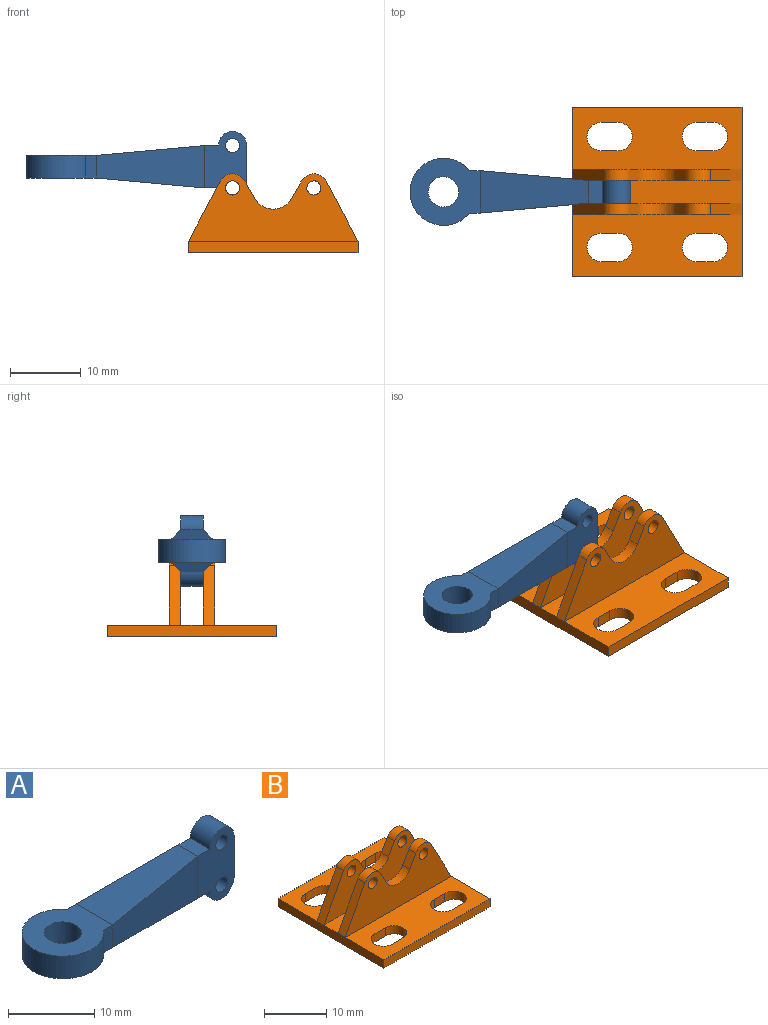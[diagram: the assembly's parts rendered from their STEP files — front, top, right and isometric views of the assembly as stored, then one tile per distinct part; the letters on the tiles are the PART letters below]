
ASSEMBLY  parts=2 mates=1
PART A: 19 faces, bbox 31.3x9.5x10 mm
  f0: plane 3.2x1.5mm, normal (0,-1,0), area 4.8mm2, adj f3,f4,f5,f9
  f1: plane 3.2x1.5mm, normal (0,1,0), area 4.8mm2, adj f3,f4,f5,f7
  f2: cylinder r=2.15mm len=4.3mm, axis (0,0,-1), area 43.2mm2, adj f4,f5
  f3: cylinder r=4.75mm len=9.5mm, axis (0,0,-1), area 74.7mm2, adj f0,f1,f4,f5
  f4: plane 9.93x9.5mm, normal (0,0,1), area 61mm2, adj f0,f1,f2,f3,f8
  f5: plane 9.93x9.5mm, normal (0,0,-1), area 61mm2, adj f0,f1,f2,f3,f6
  f6: plane 15.32x6mm, normal (-0.09,0,-1), area 70.8mm2, adj f5,f7,f9,f12
  f7: plane 15.32x6mm, normal (0.09,1,0), area 70.8mm2, adj f1,f6,f8,f18
  f8: plane 15.32x6mm, normal (-0.09,0,1), area 70.8mm2, adj f4,f7,f9,f11
  f9: plane 15.32x6mm, normal (0.09,-1,0), area 70.8mm2, adj f0,f6,f8,f17
  f10: cylinder r=2mm len=4mm, axis (0,1,0), area 20.1mm2, adj f11,f14,f17,f18
  f11: plane 3.2x2mm, normal (0,0,1), area 6.4mm2, adj f8,f10,f17,f18
  f12: plane 3.2x2mm, normal (0,0,-1), area 6.4mm2, adj f6,f13,f17,f18
  f13: cylinder r=2mm len=4mm, axis (0,1,0), area 20.1mm2, adj f12,f14,f17,f18
  f14: plane 6x3.2mm, normal (1,0,0), area 19.2mm2, adj f10,f13,f17,f18
  f15: cylinder r=1mm len=3.2mm, axis (0,1,0), area 20.1mm2, adj f17,f18
  f16: cylinder r=1mm len=3.2mm, axis (0,1,0), area 20.1mm2, adj f17,f18
  f17: plane 10x6mm, normal (0,-1,0), area 42.3mm2, adj f9,f10,f11,f12,f13,f14,f15,f16
  f18: plane 10x6mm, normal (0,1,0), area 42.3mm2, adj f7,f10,f11,f12,f13,f14,f15,f16
PART B: 46 faces, bbox 24x24x11.2 mm
  f0: plane 24x9.55mm, normal (0,1,0), area 143.1mm2, adj f4,f37,f38,f39,f40,f41,f42,f43
  f1: plane 24x9.55mm, normal (0,-1,0), area 143.1mm2, adj f5,f37,f38,f39,f40,f41,f42,f43
  f2: plane 24x9.55mm, normal (0,-1,0), area 143.1mm2, adj f4,f28,f29,f30,f31,f32,f33,f34
  f3: plane 24x9.55mm, normal (0,1,0), area 143.1mm2, adj f26,f28,f29,f30,f31,f32,f33,f34
  f4: plane 24x3.2mm, normal (0,0,1), area 76.8mm2, adj f0,f2,f12,f14
  f5: plane 24x8.8mm, normal (0,0,1), area 166.9mm2, adj f1,f9,f10,f11,f12,f14,f15,f16
  f6: plane 2.34x1.6mm, normal (0,1,0), area 3.7mm2, adj f7,f25,f26,f27
  f7: cylinder r=2mm len=4mm, axis (0,0,-1), area 10.2mm2, adj f6,f8,f26,f27
  f8: plane 2.4x1.6mm, normal (0,-1,0), area 3.8mm2, adj f7,f25,f26,f27
  f9: plane 2.34x1.6mm, normal (0,-1,0), area 3.7mm2, adj f5,f10,f21,f27
  f10: cylinder r=2mm len=4mm, axis (0,0,-1), area 10.2mm2, adj f5,f9,f11,f27
  f11: plane 2.4x1.6mm, normal (0,1,0), area 3.8mm2, adj f5,f10,f21,f27
  f12: plane 24x1.6mm, normal (1,0,0), area 38.4mm2, adj f4,f5,f13,f22,f26,f27,f34,f37
  f13: plane 24x1.6mm, normal (0,1,0), area 38.4mm2, adj f12,f14,f26,f27
  f14: plane 24x1.6mm, normal (-1,0,0), area 38.4mm2, adj f4,f5,f13,f22,f26,f27,f33,f38
  f15: cylinder r=2mm len=4mm, axis (0,0,-1), area 10.2mm2, adj f5,f16,f23,f27
  f16: plane 2.34x1.6mm, normal (0,-1,0), area 3.7mm2, adj f5,f15,f17,f27
  f17: cylinder r=2mm len=4mm, axis (0,0,-1), area 10.1mm2, adj f5,f16,f23,f27
  f18: cylinder r=2mm len=4mm, axis (0,0,-1), area 10.2mm2, adj f19,f24,f26,f27
  f19: plane 2.34x1.6mm, normal (0,1,0), area 3.7mm2, adj f18,f20,f26,f27
  f20: cylinder r=2mm len=4mm, axis (0,0,-1), area 10.1mm2, adj f19,f24,f26,f27
  f21: cylinder r=2mm len=4mm, axis (0,0,-1), area 10.1mm2, adj f5,f9,f11,f27
  f22: plane 24x1.6mm, normal (0,-1,0), area 38.4mm2, adj f5,f12,f14,f27
  f23: plane 2.4x1.6mm, normal (0,1,0), area 3.8mm2, adj f5,f15,f17,f27
  f24: plane 2.4x1.6mm, normal (0,-1,0), area 3.8mm2, adj f18,f20,f26,f27
  f25: cylinder r=2mm len=4mm, axis (0,0,-1), area 10.1mm2, adj f6,f8,f26,f27
  f26: plane 24x8.8mm, normal (0,0,1), area 166.9mm2, adj f3,f6,f7,f8,f12,f13,f14,f18
  f27: plane 24x24mm, normal (0,0,-1), area 487.3mm2, adj f6,f7,f8,f9,f10,f11,f12,f13
  f28: cylinder r=2mm len=3.51mm, axis (0,-1,0), area 6.8mm2, adj f2,f3,f29,f34
  f29: plane 2.47x1.6mm, normal (-0.87,0,0.49), area 4.5mm2, adj f2,f3,f28,f30
  f30: cylinder r=3mm len=5.22mm, axis (0,-1,0), area 10.1mm2, adj f2,f3,f29,f31
  f31: plane 2.47x1.6mm, normal (0.87,0,0.49), area 4.5mm2, adj f2,f3,f30,f32
  f32: cylinder r=2mm len=3.51mm, axis (0,-1,0), area 6.8mm2, adj f2,f3,f31,f33
  f33: plane 8.48x4.48mm, normal (-0.88,0,0.47), area 15.4mm2, adj f2,f3,f14,f32
  f34: plane 8.48x4.48mm, normal (0.88,0,0.47), area 15.4mm2, adj f2,f3,f12,f28
  f35: cylinder r=1mm len=2mm, axis (0,-1,0), area 10.1mm2, adj f2,f3
  f36: cylinder r=1mm len=2mm, axis (0,-1,0), area 10.1mm2, adj f2,f3
  f37: plane 8.48x4.48mm, normal (0.88,0,0.47), area 15.4mm2, adj f0,f1,f12,f43
  f38: plane 8.48x4.48mm, normal (-0.88,0,0.47), area 15.4mm2, adj f0,f1,f14,f39
  f39: cylinder r=2mm len=3.51mm, axis (0,-1,0), area 6.8mm2, adj f0,f1,f38,f40
  f40: plane 2.47x1.6mm, normal (0.87,0,0.49), area 4.5mm2, adj f0,f1,f39,f41
  f41: cylinder r=3mm len=5.22mm, axis (0,-1,0), area 10.1mm2, adj f0,f1,f40,f42
  f42: plane 2.47x1.6mm, normal (-0.87,0,0.49), area 4.5mm2, adj f0,f1,f41,f43
  f43: cylinder r=2mm len=3.51mm, axis (0,-1,0), area 6.8mm2, adj f0,f1,f37,f42
  f44: cylinder r=1mm len=2mm, axis (0,-1,0), area 10.1mm2, adj f0,f1
  f45: cylinder r=1mm len=2mm, axis (0,-1,0), area 10.1mm2, adj f0,f1
PLACE A t=(0,0,-6.85)mm
PLACE B at identity fixed
MATE revolute B.f32 <-> A.f13  axis (0,-1,0) through (-5.75,-1.6,9.15)mm
